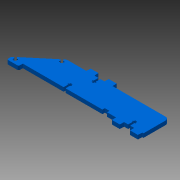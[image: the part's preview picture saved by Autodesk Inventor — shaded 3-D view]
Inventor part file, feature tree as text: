
AUTODESK INVENTOR PART (.ipt)
format: ipt  version: 2013 (Build 170138000, 138)  size: 175,104 bytes
history: native  units: mm
features: extrude x1, sketch x1
ambient origin geometry x8: Origin, YZ Plane, XZ Plane, XY Plane, X Axis, Y Axis, Z Axis, Center Point
bodies: Solid1 (feature_tree)
feature tree (2):
  extrude  "Extrusion1"  [1 undecoded]
  sketch  "Sketch1"  dims[d0=6.0mm d1=0.0mm]
note: 1 required parameter value undecoded (feature->parameter linkage not recoverable at this tier; creation-order binding heuristic only, values carry confidence <= 0.55)
